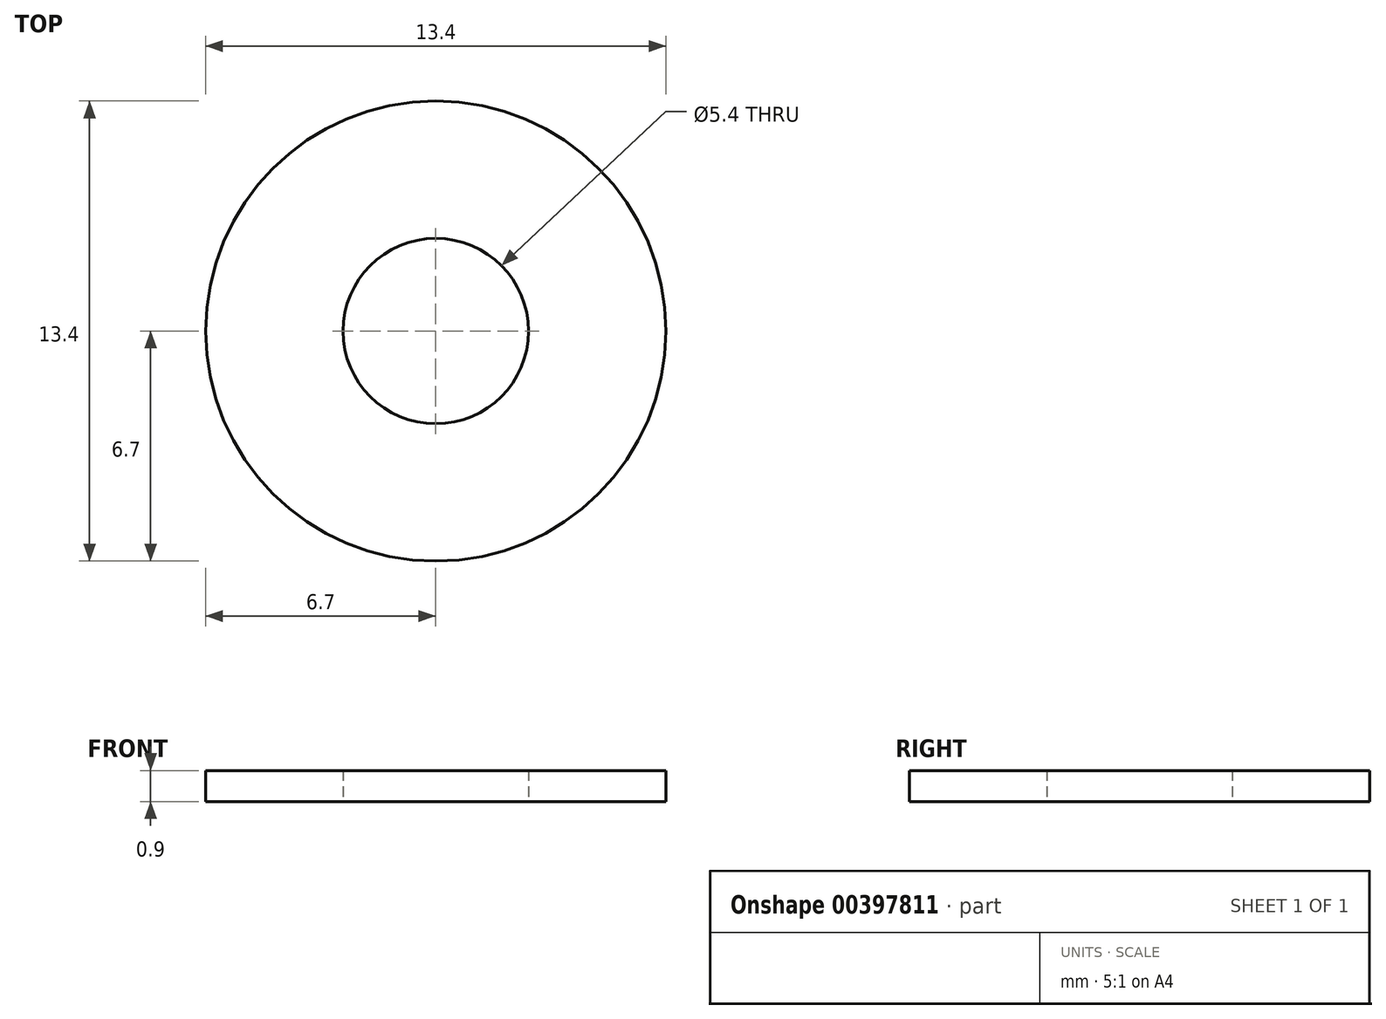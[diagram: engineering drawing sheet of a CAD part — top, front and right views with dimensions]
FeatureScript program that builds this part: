
annotation { "Feature Type Name" : "Feature", "Feature Type Description" : "" }
export const myFeature = defineFeature(function(context is Context, id is Id, definition is map)
    precondition{}
    {
        {
            var Q0;
            Q0=qCreatedBy(makeId("Top.planeOp"),FACE);
            var sketch = newSketch(context, id + "F0", { "sketchPlane" : qUnion([Q0])});
            skCircle(sketch, "E0", {"center": v(0, 0) * mm, "radius": 6.7 * mm});
            skCircle(sketch, "E1", {"center": v(0, 0) * mm, "radius": 2.7 * mm});
            skSolve(sketch);
        }
        {
            var Q0;
            Q0=makeQuery(id+"F0.imprint","IMPRINT",FACE,{"disambiguationData":[TD([[makeQuery(id+"F0.imprint","IMPRINT",EDGE,{"derivedFrom":sQuery(id+"F0.wireOp",EDGE,"E0")}),1.0]])]});
            extrude(context, id + "F1", {"entities" : qUnion([Q0]), "depth" : 0.9 * mm});
        }
    });
